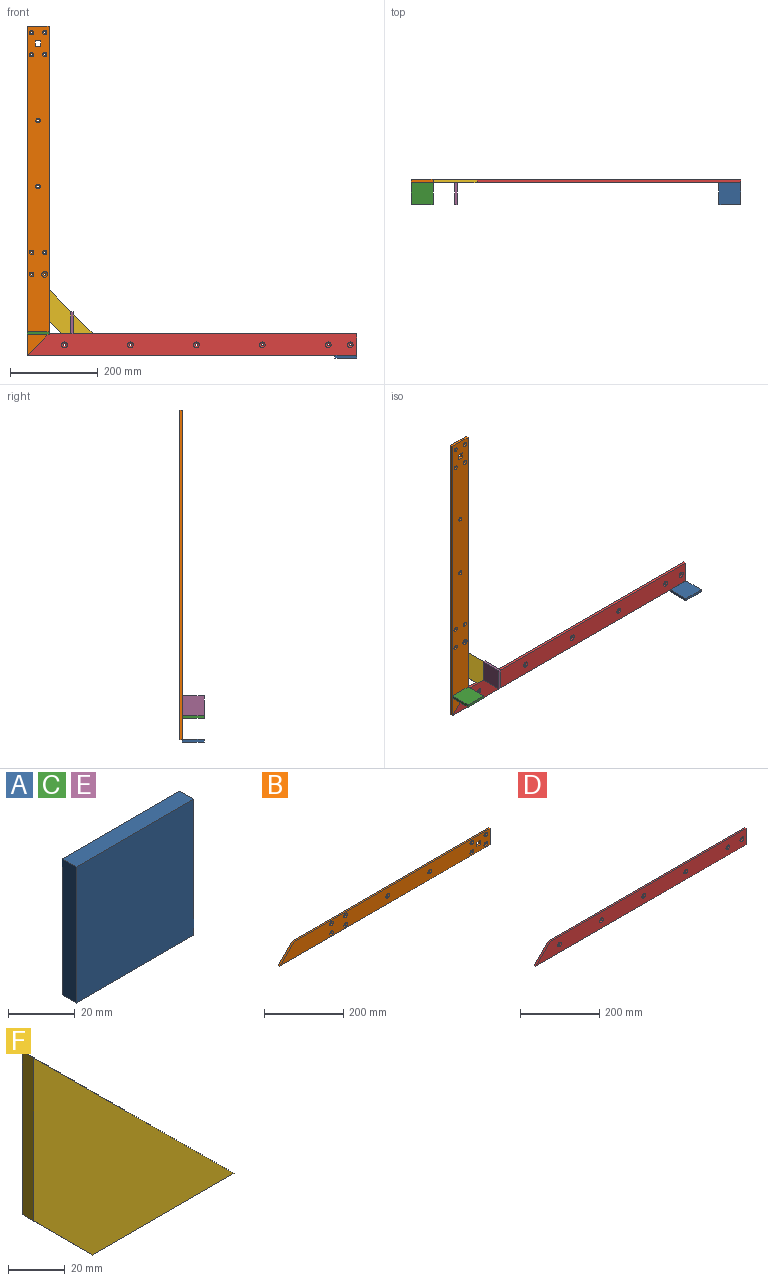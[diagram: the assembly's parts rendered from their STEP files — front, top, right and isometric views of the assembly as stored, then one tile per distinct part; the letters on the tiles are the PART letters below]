
ASSEMBLY  parts=6 mates=5
PART A: 6 faces, bbox 50x6x50 mm
  f0: plane 50x6mm, normal (1,0,0), area 300mm2, adj f1,f3,f4,f5
  f1: plane 50x6mm, normal (0,0,1), area 300mm2, adj f0,f2,f4,f5
  f2: plane 50x6mm, normal (-1,0,0), area 300mm2, adj f1,f3,f4,f5
  f3: plane 50x6mm, normal (0,0,-1), area 300mm2, adj f0,f2,f4,f5
  f4: plane 50x50mm, normal (0,-1,0), area 2500mm2, adj f0,f1,f2,f3
  f5: plane 50x50mm, normal (0,1,0), area 2500mm2, adj f0,f1,f2,f3
PART B: 40 faces, bbox 750x6x50 mm
  f0: plane 13x6mm, normal (0,0,-1), area 78mm2, adj f1,f17,f18,f19
  f1: plane 13x6mm, normal (-1,0,0), area 78mm2, adj f0,f2,f18,f19
  f2: plane 13x6mm, normal (0,0,1), area 78mm2, adj f1,f17,f18,f19
  f3: plane 50x6mm, normal (1,0,0), area 300mm2, adj f4,f16,f18,f19
  f4: plane 700x6mm, normal (0,0,1), area 4200mm2, adj f3,f5,f18,f19
  f5: plane 50x50mm, normal (-0.71,0,0.71), area 424.3mm2, adj f4,f16,f18,f19
  f6: cylinder r=3mm len=6mm, axis (0,1,0), area 10.1mm2, adj f25,f34
  f7: cylinder r=3mm len=6mm, axis (0,1,0), area 10.1mm2, adj f24,f35
  f8: cylinder r=3mm len=6mm, axis (0,1,0), area 10.1mm2, adj f21,f37
  f9: cylinder r=3mm len=6mm, axis (0,1,0), area 37.7mm2, adj f20,f39
  f10: cylinder r=3mm len=6mm, axis (0,1,0), area 10.1mm2, adj f23,f36
  f11: cylinder r=3mm len=6mm, axis (0,1,0), area 10.1mm2, adj f22,f38
  f12: cylinder r=3mm len=6mm, axis (0,1,0), area 10.1mm2, adj f28,f32
  f13: cylinder r=3mm len=6mm, axis (0,1,0), area 10.1mm2, adj f26,f33
  f14: cylinder r=3mm len=6mm, axis (0,1,0), area 10.1mm2, adj f29,f30
  f15: cylinder r=3mm len=6mm, axis (0,1,0), area 10.1mm2, adj f27,f31
  f16: plane 750x6mm, normal (0,0,-1), area 4500mm2, adj f3,f5,f18,f19
  f17: plane 13x6mm, normal (1,0,0), area 78mm2, adj f0,f2,f18,f19
  f18: plane 750x50mm, normal (0,-1,0), area 34768.3mm2, adj f0,f1,f2,f3,f4,f5,f16,f17
  f19: plane 750x50mm, normal (0,1,0), area 35242.9mm2, adj f0,f1,f2,f3,f4,f5,f16,f17
  f20: cone r=6.46mm half-angle=60deg, axis (0,1,0), area 118.9mm2, adj f9,f19
  f21: cone r=5mm half-angle=30deg, axis (0,1,0), area 100.5mm2, adj f8,f19
  f22: cone r=5mm half-angle=30deg, axis (0,1,0), area 100.5mm2, adj f11,f19
  f23: cone r=5mm half-angle=30deg, axis (0,1,0), area 100.5mm2, adj f10,f19
  f24: cone r=5mm half-angle=30deg, axis (0,1,0), area 100.5mm2, adj f7,f19
  f25: cone r=5mm half-angle=30deg, axis (0,1,0), area 100.5mm2, adj f6,f19
  f26: cone r=5mm half-angle=30deg, axis (0,1,0), area 100.5mm2, adj f13,f19
  f27: cone r=5mm half-angle=30deg, axis (0,1,0), area 100.5mm2, adj f15,f19
  f28: cone r=5mm half-angle=30deg, axis (0,1,0), area 100.5mm2, adj f12,f19
  f29: cone r=5mm half-angle=30deg, axis (0,1,0), area 100.5mm2, adj f14,f19
  f30: cone r=3mm half-angle=60deg, axis (0,-1,0), area 118.9mm2, adj f14,f18
  f31: cone r=3mm half-angle=60deg, axis (0,-1,0), area 118.9mm2, adj f15,f18
  f32: cone r=3mm half-angle=60deg, axis (0,-1,0), area 118.9mm2, adj f12,f18
  f33: cone r=3mm half-angle=60deg, axis (0,-1,0), area 118.9mm2, adj f13,f18
  f34: cone r=3mm half-angle=60deg, axis (0,-1,0), area 118.9mm2, adj f6,f18
  f35: cone r=3mm half-angle=60deg, axis (0,-1,0), area 118.9mm2, adj f7,f18
  f36: cone r=3mm half-angle=60deg, axis (0,-1,0), area 118.9mm2, adj f10,f18
  f37: cone r=3mm half-angle=60deg, axis (0,-1,0), area 118.9mm2, adj f8,f18
  f38: cone r=3mm half-angle=60deg, axis (0,-1,0), area 118.9mm2, adj f11,f18
  f39: cone r=3mm half-angle=60deg, axis (0,-1,0), area 118.9mm2, adj f9,f18
PART C: same geometry as A
PART D: 24 faces, bbox 750x6x50 mm
  f0: plane 50x6mm, normal (1,0,0), area 300mm2, adj f1,f8,f10,f11
  f1: plane 700x6mm, normal (0,0,1), area 4200mm2, adj f0,f2,f10,f11
  f2: plane 50x50mm, normal (-0.71,0,0.71), area 424.3mm2, adj f1,f8,f10,f11
  f3: cylinder r=3mm len=6mm, axis (0,1,0), area 10.1mm2, adj f18,f19
  f4: cylinder r=3mm len=6mm, axis (0,1,0), area 10.1mm2, adj f14,f15
  f5: cylinder r=3mm len=6mm, axis (0,1,0), area 10.1mm2, adj f12,f13
  f6: cylinder r=3mm len=6mm, axis (0,1,0), area 37.7mm2, adj f22,f23
  f7: cylinder r=3mm len=6mm, axis (0,1,0), area 10.1mm2, adj f20,f21
  f8: plane 750x6mm, normal (0,0,-1), area 4500mm2, adj f0,f2,f10,f11
  f9: cylinder r=3mm len=6mm, axis (0,1,0), area 10.1mm2, adj f16,f17
  f10: plane 750x50mm, normal (0,-1,0), area 35462.4mm2, adj f0,f1,f2,f8,f12,f14,f16,f18
  f11: plane 750x50mm, normal (0,1,0), area 35726mm2, adj f0,f1,f2,f8,f13,f15,f17,f19
  f12: cone r=3mm half-angle=60deg, axis (0,-1,0), area 118.9mm2, adj f5,f10
  f13: cone r=5mm half-angle=30deg, axis (0,1,0), area 100.5mm2, adj f5,f11
  f14: cone r=3mm half-angle=60deg, axis (0,-1,0), area 118.9mm2, adj f4,f10
  f15: cone r=5mm half-angle=30deg, axis (0,1,0), area 100.5mm2, adj f4,f11
  f16: cone r=3mm half-angle=60deg, axis (0,-1,0), area 118.9mm2, adj f9,f10
  f17: cone r=5mm half-angle=30deg, axis (0,1,0), area 100.5mm2, adj f9,f11
  f18: cone r=3mm half-angle=60deg, axis (0,-1,0), area 118.9mm2, adj f3,f10
  f19: cone r=5mm half-angle=30deg, axis (0,1,0), area 100.5mm2, adj f3,f11
  f20: cone r=5mm half-angle=30deg, axis (0,1,0), area 100.5mm2, adj f7,f11
  f21: cone r=3mm half-angle=60deg, axis (0,-1,0), area 118.9mm2, adj f7,f10
  f22: cone r=6.46mm half-angle=60deg, axis (0,1,0), area 118.9mm2, adj f6,f11
  f23: cone r=3mm half-angle=60deg, axis (0,-1,0), area 118.9mm2, adj f6,f10
PART E: same geometry as A
PART F: 6 faces, bbox 100x6x100 mm
  f0: plane 100x100mm, normal (0.71,0,0.71), area 848.5mm2, adj f1,f3,f4,f5
  f1: plane 70.71x6mm, normal (-1,0,0), area 424.3mm2, adj f0,f2,f4,f5
  f2: plane 29.29x29.29mm, normal (-0.71,0,-0.71), area 248.5mm2, adj f1,f3,f4,f5
  f3: plane 70.71x6mm, normal (0,0,-1), area 424.3mm2, adj f0,f2,f4,f5
  f4: plane 100x100mm, normal (0,-1,0), area 4571.1mm2, adj f0,f1,f2,f3
  f5: plane 100x100mm, normal (0,1,0), area 4571.1mm2, adj f0,f1,f2,f3
PLACE A rot(axis=(1,0,0),90deg) t=(335.45,-28.5,-250.47)mm
PLACE B rot(axis=(0.71,0,0.71),180deg) t=(-364.55,-0.5,126.53)mm fixed
PLACE C rot(axis=(1,0,0),90deg) t=(-364.55,-28.5,-196.47)mm
PLACE D t=(-14.55,-0.5,-223.47)mm
PLACE E rot(axis=(0,0,-1),90deg) t=(-287.55,-28.5,-173.47)mm
PLACE F t=(-289.55,-0.5,-148.47)mm
MATE fastened F.f1 <-> B.f4  axis (-1,0,0) through (-339.55,-0.5,-98.47)mm
MATE fastened E.f2 <-> B.f19  axis (0,1,0) through (-290.55,-3.5,-198.47)mm
MATE fastened D.f2 <-> B.f5  axis (-0.71,0,0.71) through (-364.55,-0.5,-223.47)mm
MATE fastened C.f3 <-> B.f19  axis (0,1,0) through (-389.55,-3.5,-199.47)mm
MATE fastened D.f10 <-> A.f3  axis (0,-1,0) through (335.45,-3.5,-247.47)mm
